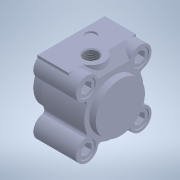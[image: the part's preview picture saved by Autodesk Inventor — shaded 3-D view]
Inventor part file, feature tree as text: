
AUTODESK INVENTOR PART (.ipt)
format: ipt  version: 2024.3 (Build 283343000, 343)  size: 321,536 bytes
history: native  units: mm
features: other x21, sketch x9, extrude x5, pattern_linear x3, revolve x2, hole x2, thread x1
ambient origin geometry x8: Origin, YZ Plane, XZ Plane, XY Plane, X Axis, Y Axis, Z Axis, Center Point
bodies: Solid1 (feature_tree)
feature tree (43):
  extrude  "Extrusion1"  Depth=32.5mm TaperAngle=0.0deg
  extrude  "Extrusion2"  TaperAngle=360.0deg  [1 undecoded]
  extrude  "Extrusion3"  Depth=20.0mm TaperAngle=0.0deg
  revolve  "Revolution1"  Angle=360.0deg
  hole  "Hole1"  [1 undecoded]
  extrude  "Extrusion4"  Depth=20.0mm
  pattern_linear  "Rectangular Pattern1"  [2 undecoded]
  revolve  "Revolution2"  [1 undecoded]
  thread  "Thread1"  [1 undecoded]
  pattern_linear  "Rectangular Pattern2"  [2 undecoded]
  extrude  "Extrusion5"  [1 undecoded]
  pattern_linear  "Rectangular Pattern3"  [2 undecoded]
  hole  "Hole2"  [1 undecoded]
  other  "accessories_XY"
  other  "accessories_YZ"
  other  "accessories_ZX"
  other  "accessories_X"
  other  "accessories_Y"
  other  "accessories_Z"
  other  "accessories_Center"
  other  "br_r_XY"
  other  "br_r_YZ"
  other  "br_r_ZX"
  other  "br_r_X"
  other  "br_r_Y"
  other  "br_r_Z"
  other  "br_r_Center"
  other  "fitting_XY"
  other  "fitting_YZ"
  other  "fitting_ZX"
  other  "fitting_X"
  other  "fitting_Y"
  other  "fitting_Z"
  other  "fitting_Center"
  sketch  "Sketch_1"  dims[d0=26.0mm d1=0.0mm d2=32.5mm d3=0.0mm]
  sketch  "Sketch_2"  dims[d4=8.0mm d5=0.0mm d6=360.0deg]
  sketch  "Sketch_3"  dims[d7=6.5mm d8=6.0mm d9=4.0mm d10=2.0mm d11=90.0deg d12=1.0mm d13=0.0mm d14=20.0mm d15=0.0mm]
  sketch  "Sketch_4"  dims[d16=20.0mm d18=32.5mm d19=20.0mm d21=32.5mm d22=360.0deg]
  sketch  "Sketch5"  dims[d23=9.4585mm d24=0.0mm d25=20.0mm d27=32.5mm d28=20.0mm d30=32.5mm]
  sketch  "Sketch_6"  dims[d31=4.5mm d32=0.0mm d33=20.0mm d35=32.5mm d36=20.0mm d38=32.5mm]
  sketch  "Sketch_8"  dims[d39=8.0mm d40=7.4mm d41=0.624793mm d42=7.985mm d43=9.728mm d44=2.0mm d45=90.0deg d46=10.0mm d47=120.0deg]
  sketch  "Sketch_10"
  sketch  "Sketch9"  dims[d48=0.0mm d49=0.0mm d50=0.0mm]
note: 12 required parameter values undecoded (feature->parameter linkage not recoverable at this tier; creation-order binding heuristic only, values carry confidence <= 0.55)
